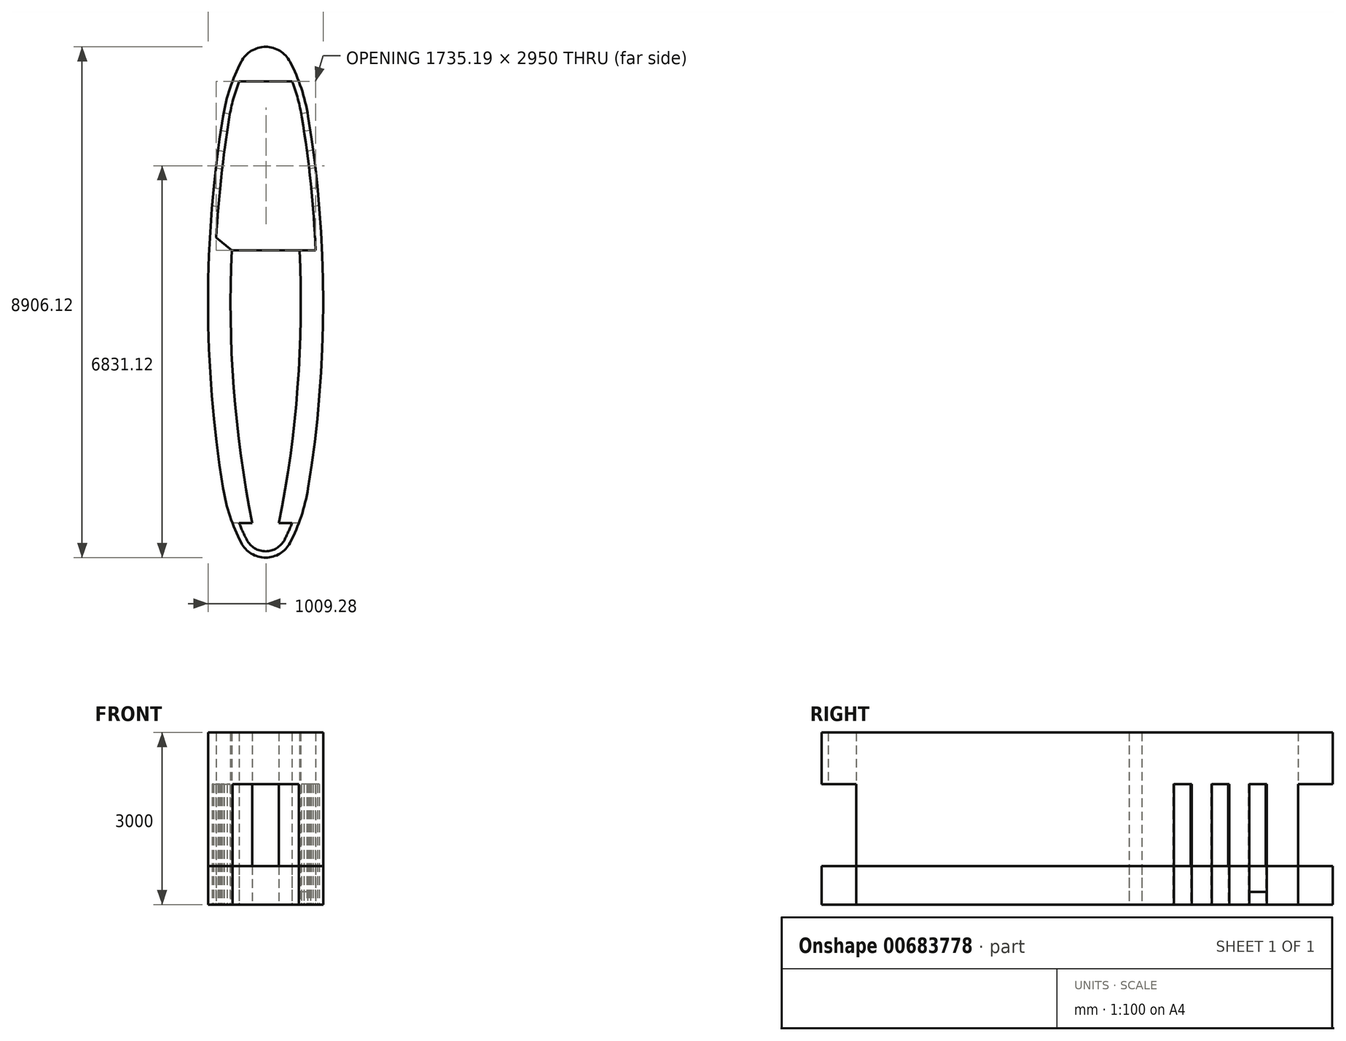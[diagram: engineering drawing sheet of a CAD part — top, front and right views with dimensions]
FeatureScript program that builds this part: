
annotation { "Feature Type Name" : "Feature", "Feature Type Description" : "" }
export const myFeature = defineFeature(function(context is Context, id is Id, definition is map)
    precondition{}
    {
        {
            var Q0;
            Q0=qCreatedBy(makeId("Top.planeOp"),FACE);
            var sketch = newSketch(context, id + "F0", { "sketchPlane" : qUnion([Q0])});
            skLineSegment(sketch, "E0", {"start": v(0, 4453.06) * mm, "end": v(0, -4453.06) * mm, "construction": true});
            skArc(sketch, "E1", {"start": v(426.3, 4193.68) * mm, "mid": v(249.5, 4383.12) * mm, "end": v(0, 4453.06) * mm});
            skArc(sketch, "E2", {"start": v(426.3, 4193.68) * mm, "mid": v(620.98, 3731.45) * mm, "end": v(740.57, 3244.35) * mm});
            skArc(sketch, "E3", {"start": v(740.57, 3244.35) * mm, "mid": v(937.75, 1627.5) * mm, "end": v(1003.62, 0) * mm});
            skArc(sketch, "E4.0", {"start": v(328.6, 4143.13) * mm, "mid": v(192.32, 4289.15) * mm, "end": v(0, 4343.06) * mm});
            skArc(sketch, "E4.1", {"start": v(328.6, 4143.13) * mm, "mid": v(516.55, 3696.88) * mm, "end": v(632, 3226.63) * mm});
            skArc(sketch, "E4.2", {"start": v(632, 3226.63) * mm, "mid": v(786.52, 2068.53) * mm, "end": v(873.24, 903.4) * mm});
            skLineSegment(sketch, "E5", {"start": v(1003.62, 0) * mm, "end": v(-1003.62, 0) * mm, "construction": true});
            skArc(sketch, "E6.MirrorCS", {"start": v(-740.57, 3244.35) * mm, "mid": v(-937.75, 1627.5) * mm, "end": v(-1003.62, 0) * mm});
            skArc(sketch, "E7.MirrorCS", {"start": v(-328.6, 4143.13) * mm, "mid": v(-516.55, 3696.88) * mm, "end": v(-632, 3226.63) * mm});
            skArc(sketch, "E8.MirrorCS", {"start": v(-426.3, 4193.68) * mm, "mid": v(-620.98, 3731.45) * mm, "end": v(-740.57, 3244.35) * mm});
            skArc(sketch, "E9.MirrorCS", {"start": v(-328.6, 4143.13) * mm, "mid": v(-192.32, 4289.15) * mm, "end": v(0, 4343.06) * mm});
            skArc(sketch, "E10.MirrorCS", {"start": v(-426.3, 4193.68) * mm, "mid": v(-249.5, 4383.12) * mm, "end": v(0, 4453.06) * mm});
            skLineSegment(sketch, "E11.MirrorCS", {"start": v(-1003.62, 0) * mm, "end": v(1003.62, 0) * mm, "construction": true});
            skArc(sketch, "E12.MirrorCS", {"start": v(-632, 3226.63) * mm, "mid": v(-786.53, 2068.37) * mm, "end": v(-873.25, 903.06) * mm});
            skArc(sketch, "E13.MirrorCS", {"start": v(632, -3226.63) * mm, "mid": v(828.11, -1618.61) * mm, "end": v(893.62, 0) * mm});
            skArc(sketch, "E14.MirrorCS", {"start": v(740.57, -3244.35) * mm, "mid": v(937.75, -1627.5) * mm, "end": v(1003.62, 0) * mm});
            skArc(sketch, "E15.MirrorCS", {"start": v(-632, -3226.63) * mm, "mid": v(-828.11, -1618.61) * mm, "end": v(-893.62, 0) * mm});
            skArc(sketch, "E16.MirrorCS", {"start": v(-740.57, -3244.35) * mm, "mid": v(-937.75, -1627.5) * mm, "end": v(-1003.62, 0) * mm});
            skArc(sketch, "E17.MirrorCS", {"start": v(328.6, -4143.13) * mm, "mid": v(516.55, -3696.88) * mm, "end": v(632, -3226.63) * mm});
            skArc(sketch, "E18.MirrorCS", {"start": v(426.3, -4193.68) * mm, "mid": v(620.98, -3731.45) * mm, "end": v(740.57, -3244.35) * mm});
            skArc(sketch, "E19.MirrorCS", {"start": v(-426.3, -4193.68) * mm, "mid": v(-620.98, -3731.45) * mm, "end": v(-740.57, -3244.35) * mm});
            skArc(sketch, "E20.MirrorCS", {"start": v(-328.6, -4143.13) * mm, "mid": v(-516.55, -3696.88) * mm, "end": v(-632, -3226.63) * mm});
            skArc(sketch, "E21.MirrorCS", {"start": v(-426.3, -4193.68) * mm, "mid": v(-249.5, -4383.12) * mm, "end": v(0, -4453.06) * mm});
            skArc(sketch, "E22.MirrorCS", {"start": v(-328.6, -4143.13) * mm, "mid": v(-192.32, -4289.15) * mm, "end": v(0, -4343.06) * mm});
            skArc(sketch, "E23.MirrorCS", {"start": v(328.6, -4143.13) * mm, "mid": v(192.32, -4289.15) * mm, "end": v(0, -4343.06) * mm});
            skArc(sketch, "E24.MirrorCS", {"start": v(426.3, -4193.68) * mm, "mid": v(249.5, -4383.12) * mm, "end": v(0, -4453.06) * mm});
            skLineSegment(sketch, "E25", {"start": v(577.97, 3853.06) * mm, "end": v(-577.97, 3853.06) * mm});
            skLineSegment(sketch, "E26", {"start": v(730.42, 3303.06) * mm, "end": v(621.9, 3285) * mm});
            skLineSegment(sketch, "E27", {"start": v(779.38, 2996.95) * mm, "end": v(670.86, 2978.88) * mm});
            skLineSegment(sketch, "E28", {"start": v(828.45, 2650.4) * mm, "end": v(719.89, 2632.34) * mm});
            skLineSegment(sketch, "E29", {"start": v(866.88, 2342.8) * mm, "end": v(758.25, 2324.72) * mm});
            skLineSegment(sketch, "E30", {"start": v(904.58, 1994.84) * mm, "end": v(795.83, 1976.74) * mm});
            skLineSegment(sketch, "E31", {"start": v(932.91, 1686.13) * mm, "end": v(824.04, 1668.03) * mm});
            skLineSegment(sketch, "E32.MirrorCS", {"start": v(-932.91, 1686.13) * mm, "end": v(-824.04, 1668.03) * mm});
            skLineSegment(sketch, "E33.MirrorCS", {"start": v(-904.58, 1994.84) * mm, "end": v(-795.83, 1976.74) * mm});
            skLineSegment(sketch, "E34.MirrorCS", {"start": v(-866.88, 2342.8) * mm, "end": v(-758.25, 2324.72) * mm});
            skLineSegment(sketch, "E35.MirrorCS", {"start": v(-828.45, 2650.4) * mm, "end": v(-719.89, 2632.34) * mm});
            skLineSegment(sketch, "E36.MirrorCS", {"start": v(-730.42, 3303.06) * mm, "end": v(-621.9, 3285) * mm});
            skLineSegment(sketch, "E37.MirrorCS", {"start": v(-779.38, 2996.95) * mm, "end": v(-670.86, 2978.88) * mm});
            skLineSegment(sketch, "E38", {"start": v(-873.25, 903.06) * mm, "end": v(-873.25, 903.06) * mm});
            skArc(sketch, "E39", {"start": v(873.24, 903.4) * mm, "mid": v(888.52, 451.81) * mm, "end": v(893.62, 0) * mm});
            skLineSegment(sketch, "E40", {"start": v(-873.25, 903.06) * mm, "end": v(873.25, 903.06) * mm});
            skArc(sketch, "E41", {"start": v(-873.25, 903.06) * mm, "mid": v(-888.53, 451.65) * mm, "end": v(-893.62, 0) * mm});
            skArc(sketch, "E42.0", {"start": v(-591.96, 903.06) * mm, "mid": v(-607.46, 451.65) * mm, "end": v(-612.62, 0) * mm});
            skArc(sketch, "E43.0", {"start": v(591.96, 903.06) * mm, "mid": v(607.46, 451.65) * mm, "end": v(612.62, 0) * mm});
            skArc(sketch, "E44.0", {"start": v(233.08, -3853.06) * mm, "mid": v(517.5, -1935.85) * mm, "end": v(612.62, 0) * mm});
            skArc(sketch, "E45.0", {"start": v(-233.08, -3853.06) * mm, "mid": v(-517.5, -1935.85) * mm, "end": v(-612.62, 0) * mm});
            skLineSegment(sketch, "E46", {"start": v(591.96, 903.06) * mm, "end": v(967.05, 1213.06) * mm});
            skLineSegment(sketch, "E47.MirrorCS", {"start": v(-591.96, 903.06) * mm, "end": v(-967.05, 1213.06) * mm});
            skLineSegment(sketch, "E48.MirrorCS", {"start": v(577.97, -3853.06) * mm, "end": v(-577.97, -3853.06) * mm});
            skSolve(sketch);
        }
        {
            var Q0;
            {var subQ20=sQuery(id+"F0.wireOp",EDGE,"E4.1");var subQ21=makeQuery(id+"F0.imprint","INTERSECT",VERTEX,{"derivedFrom":[subQ20,sQuery(id+"F0.wireOp",EDGE,"E26")]});Q0=makeQuery(id+"F0.imprint","IMPRINT",FACE,{"disambiguationData":[TD([[makeQuery(id+"F0.imprint","IMPRINT",EDGE,{"disambiguationData":[TD([[subQ21,1.0]])],"derivedFrom":subQ20}),-1.0]])]});}
            extrude(context, id + "F1", {"entities" : qUnion([Q0]), "depth" : 220 * mm, "offsetDistance" : 25 * mm});
        }
        {
            var Q0;
            {var subQ0=sQuery(id+"F0.wireOp",EDGE,"E30");Q0=makeQuery(id+"F0.imprint","IMPRINT",FACE,{"disambiguationData":[TD([[makeQuery(id+"F0.imprint","IMPRINT",EDGE,{"derivedFrom":subQ0}),1.0]])]});}
            var Q1;
            {var subQ0=sQuery(id+"F0.wireOp",EDGE,"E28");Q1=makeQuery(id+"F0.imprint","IMPRINT",FACE,{"disambiguationData":[TD([[makeQuery(id+"F0.imprint","IMPRINT",EDGE,{"derivedFrom":subQ0}),1.0]])]});}
            var Q2;
            {var subQ0=sQuery(id+"F0.wireOp",EDGE,"E29");Q2=makeQuery(id+"F0.imprint","IMPRINT",FACE,{"disambiguationData":[TD([[makeQuery(id+"F0.imprint","IMPRINT",EDGE,{"derivedFrom":subQ0}),1.0]])]});}
            var Q3;
            {var subQ0=sQuery(id+"F0.wireOp",EDGE,"E31");Q3=makeQuery(id+"F0.imprint","IMPRINT",FACE,{"disambiguationData":[TD([[makeQuery(id+"F0.imprint","IMPRINT",EDGE,{"derivedFrom":subQ0}),1.0]])]});}
            var Q4;
            {var subQ0=sQuery(id+"F0.wireOp",EDGE,"E13.MirrorCS");Q4=makeQuery(id+"F0.imprint","IMPRINT",FACE,{"disambiguationData":[TD([[makeQuery(id+"F0.imprint","IMPRINT",EDGE,{"derivedFrom":subQ0}),-1.0]])]});}
            var Q5;
            {var subQ0=sQuery(id+"F0.wireOp",EDGE,"E39");var subQ1=sQuery(id+"F0.wireOp",EDGE,"E4.2");var subQ2=makeQuery(id+"F0.imprint","INTERSECT",VERTEX,{"derivedFrom":[subQ1,subQ0]});Q5=makeQuery(id+"F0.imprint","IMPRINT",FACE,{"disambiguationData":[TD([[makeQuery(id+"F0.imprint","IMPRINT",EDGE,{"disambiguationData":[TD([[subQ2,1.0]])],"derivedFrom":subQ1}),-1.0]])]});}
            var Q6;
            {var subQ1=sQuery(id+"F0.wireOp",EDGE,"E13.MirrorCS");Q6=makeQuery(id+"F0.imprint","IMPRINT",FACE,{"disambiguationData":[TD([[makeQuery(id+"F0.imprint","IMPRINT",EDGE,{"derivedFrom":subQ1}),1.0]])]});}
            var Q7;
            {var subQ1=sQuery(id+"F0.wireOp",EDGE,"E42.0");Q7=makeQuery(id+"F0.imprint","IMPRINT",FACE,{"disambiguationData":[TD([[makeQuery(id+"F0.imprint","IMPRINT",EDGE,{"derivedFrom":subQ1}),1.0]])]});}
            var Q8;
            {var subQ4=sQuery(id+"F0.wireOp",EDGE,"E15.MirrorCS");Q8=makeQuery(id+"F0.imprint","IMPRINT",FACE,{"disambiguationData":[TD([[makeQuery(id+"F0.imprint","IMPRINT",EDGE,{"derivedFrom":subQ4}),-1.0]])]});}
            var Q9;
            {var subQ1=sQuery(id+"F0.wireOp",EDGE,"E12.MirrorCS");var subQ3=sQuery(id+"F0.wireOp",EDGE,"E47.MirrorCS");var subQ4=makeQuery(id+"F0.imprint","INTERSECT",VERTEX,{"derivedFrom":[subQ1,subQ3]});Q9=makeQuery(id+"F0.imprint","IMPRINT",FACE,{"disambiguationData":[TD([[makeQuery(id+"F0.imprint","IMPRINT",EDGE,{"disambiguationData":[TD([[subQ4,-1.0]])],"derivedFrom":subQ1}),1.0]])]});}
            var Q10;
            {var subQ2=sQuery(id+"F0.wireOp",EDGE,"E15.MirrorCS");Q10=makeQuery(id+"F0.imprint","IMPRINT",FACE,{"disambiguationData":[TD([[makeQuery(id+"F0.imprint","IMPRINT",EDGE,{"derivedFrom":subQ2}),1.0]])]});}
            var Q11;
            {var subQ0=sQuery(id+"F0.wireOp",EDGE,"E22.MirrorCS");Q11=makeQuery(id+"F0.imprint","IMPRINT",FACE,{"disambiguationData":[TD([[makeQuery(id+"F0.imprint","IMPRINT",EDGE,{"derivedFrom":subQ0}),1.0]])]});}
            var Q12;
            {var subQ4=sQuery(id+"F0.wireOp",EDGE,"E21.MirrorCS");Q12=makeQuery(id+"F0.imprint","IMPRINT",FACE,{"disambiguationData":[TD([[makeQuery(id+"F0.imprint","IMPRINT",EDGE,{"derivedFrom":subQ4}),1.0]])]});}
            var Q13;
            {var subQ5=sQuery(id+"F0.wireOp",EDGE,"E4.0");Q13=makeQuery(id+"F0.imprint","IMPRINT",FACE,{"disambiguationData":[TD([[makeQuery(id+"F0.imprint","IMPRINT",EDGE,{"derivedFrom":subQ5}),1.0]])]});}
            var Q14;
            {var subQ5=sQuery(id+"F0.wireOp",EDGE,"E1");Q14=makeQuery(id+"F0.imprint","IMPRINT",FACE,{"disambiguationData":[TD([[makeQuery(id+"F0.imprint","IMPRINT",EDGE,{"derivedFrom":subQ5}),1.0]])]});}
            var Q15;
            {var subQ3=sQuery(id+"F0.wireOp",EDGE,"E26");Q15=makeQuery(id+"F0.imprint","IMPRINT",FACE,{"disambiguationData":[TD([[makeQuery(id+"F0.imprint","IMPRINT",EDGE,{"derivedFrom":subQ3}),-1.0]])]});}
            var Q16;
            {var subQ7=sQuery(id+"F0.wireOp",EDGE,"E26");Q16=makeQuery(id+"F0.imprint","IMPRINT",FACE,{"disambiguationData":[TD([[makeQuery(id+"F0.imprint","IMPRINT",EDGE,{"derivedFrom":subQ7}),1.0]])]});}
            var Q17;
            {var subQ0=sQuery(id+"F0.wireOp",EDGE,"E27");Q17=makeQuery(id+"F0.imprint","IMPRINT",FACE,{"disambiguationData":[TD([[makeQuery(id+"F0.imprint","IMPRINT",EDGE,{"derivedFrom":subQ0}),1.0]])]});}
            var Q18;
            {var subQ0=sQuery(id+"F0.wireOp",EDGE,"E36.MirrorCS");Q18=makeQuery(id+"F0.imprint","IMPRINT",FACE,{"disambiguationData":[TD([[makeQuery(id+"F0.imprint","IMPRINT",EDGE,{"derivedFrom":subQ0}),1.0]])]});}
            var Q19;
            {var subQ3=sQuery(id+"F0.wireOp",EDGE,"E36.MirrorCS");Q19=makeQuery(id+"F0.imprint","IMPRINT",FACE,{"disambiguationData":[TD([[makeQuery(id+"F0.imprint","IMPRINT",EDGE,{"derivedFrom":subQ3}),-1.0]])]});}
            var Q20;
            {var subQ0=sQuery(id+"F0.wireOp",EDGE,"E35.MirrorCS");Q20=makeQuery(id+"F0.imprint","IMPRINT",FACE,{"disambiguationData":[TD([[makeQuery(id+"F0.imprint","IMPRINT",EDGE,{"derivedFrom":subQ0}),1.0]])]});}
            var Q21;
            {var subQ0=sQuery(id+"F0.wireOp",EDGE,"E34.MirrorCS");Q21=makeQuery(id+"F0.imprint","IMPRINT",FACE,{"disambiguationData":[TD([[makeQuery(id+"F0.imprint","IMPRINT",EDGE,{"derivedFrom":subQ0}),1.0]])]});}
            var Q22;
            {var subQ0=sQuery(id+"F0.wireOp",EDGE,"E33.MirrorCS");Q22=makeQuery(id+"F0.imprint","IMPRINT",FACE,{"disambiguationData":[TD([[makeQuery(id+"F0.imprint","IMPRINT",EDGE,{"derivedFrom":subQ0}),1.0]])]});}
            var Q23;
            {var subQ0=sQuery(id+"F0.wireOp",EDGE,"E32.MirrorCS");Q23=makeQuery(id+"F0.imprint","IMPRINT",FACE,{"disambiguationData":[TD([[makeQuery(id+"F0.imprint","IMPRINT",EDGE,{"derivedFrom":subQ0}),1.0]])]});}
            var Q24;
            {var subQ0=sQuery(id+"F0.wireOp",EDGE,"E32.MirrorCS");Q24=makeQuery(id+"F0.imprint","IMPRINT",FACE,{"disambiguationData":[TD([[makeQuery(id+"F0.imprint","IMPRINT",EDGE,{"derivedFrom":subQ0}),-1.0]])]});}
            extrude(context, id + "F2", {"entities" : qUnion([Q0, Q1, Q2, Q3, Q4, Q5, Q6, Q7, Q8, Q9, Q10, Q11, Q12, Q13, Q14, Q15, Q16, Q17, Q18, Q19, Q20, Q21, Q22, Q23, Q24]), "depth" : 670 * mm, "offsetDistance" : 25 * mm});
        }
        {
            var Q0;
            {var subQ0=sQuery(id+"F0.wireOp",EDGE,"E31");Q0=makeQuery(id+"F0.imprint","IMPRINT",FACE,{"disambiguationData":[TD([[makeQuery(id+"F0.imprint","IMPRINT",EDGE,{"derivedFrom":subQ0}),1.0]])]});}
            var Q1;
            {var subQ0=sQuery(id+"F0.wireOp",EDGE,"E13.MirrorCS");Q1=makeQuery(id+"F0.imprint","IMPRINT",FACE,{"disambiguationData":[TD([[makeQuery(id+"F0.imprint","IMPRINT",EDGE,{"derivedFrom":subQ0}),-1.0]])]});}
            var Q2;
            {var subQ0=sQuery(id+"F0.wireOp",EDGE,"E39");var subQ1=sQuery(id+"F0.wireOp",EDGE,"E4.2");var subQ2=makeQuery(id+"F0.imprint","INTERSECT",VERTEX,{"derivedFrom":[subQ1,subQ0]});Q2=makeQuery(id+"F0.imprint","IMPRINT",FACE,{"disambiguationData":[TD([[makeQuery(id+"F0.imprint","IMPRINT",EDGE,{"disambiguationData":[TD([[subQ2,1.0]])],"derivedFrom":subQ1}),-1.0]])]});}
            var Q3;
            {var subQ1=sQuery(id+"F0.wireOp",EDGE,"E13.MirrorCS");Q3=makeQuery(id+"F0.imprint","IMPRINT",FACE,{"disambiguationData":[TD([[makeQuery(id+"F0.imprint","IMPRINT",EDGE,{"derivedFrom":subQ1}),1.0]])]});}
            var Q4;
            {var subQ4=sQuery(id+"F0.wireOp",EDGE,"E15.MirrorCS");Q4=makeQuery(id+"F0.imprint","IMPRINT",FACE,{"disambiguationData":[TD([[makeQuery(id+"F0.imprint","IMPRINT",EDGE,{"derivedFrom":subQ4}),-1.0]])]});}
            var Q5;
            {var subQ2=sQuery(id+"F0.wireOp",EDGE,"E15.MirrorCS");Q5=makeQuery(id+"F0.imprint","IMPRINT",FACE,{"disambiguationData":[TD([[makeQuery(id+"F0.imprint","IMPRINT",EDGE,{"derivedFrom":subQ2}),1.0]])]});}
            var Q6;
            {var subQ1=sQuery(id+"F0.wireOp",EDGE,"E12.MirrorCS");var subQ3=sQuery(id+"F0.wireOp",EDGE,"E47.MirrorCS");var subQ4=makeQuery(id+"F0.imprint","INTERSECT",VERTEX,{"derivedFrom":[subQ1,subQ3]});Q6=makeQuery(id+"F0.imprint","IMPRINT",FACE,{"disambiguationData":[TD([[makeQuery(id+"F0.imprint","IMPRINT",EDGE,{"disambiguationData":[TD([[subQ4,-1.0]])],"derivedFrom":subQ1}),1.0]])]});}
            var Q7;
            {var subQ0=sQuery(id+"F0.wireOp",EDGE,"E29");Q7=makeQuery(id+"F0.imprint","IMPRINT",FACE,{"disambiguationData":[TD([[makeQuery(id+"F0.imprint","IMPRINT",EDGE,{"derivedFrom":subQ0}),1.0]])]});}
            var Q8;
            {var subQ0=sQuery(id+"F0.wireOp",EDGE,"E27");Q8=makeQuery(id+"F0.imprint","IMPRINT",FACE,{"disambiguationData":[TD([[makeQuery(id+"F0.imprint","IMPRINT",EDGE,{"derivedFrom":subQ0}),1.0]])]});}
            var Q9;
            {var subQ3=sQuery(id+"F0.wireOp",EDGE,"E26");Q9=makeQuery(id+"F0.imprint","IMPRINT",FACE,{"disambiguationData":[TD([[makeQuery(id+"F0.imprint","IMPRINT",EDGE,{"derivedFrom":subQ3}),-1.0]])]});}
            var Q10;
            {var subQ0=sQuery(id+"F0.wireOp",EDGE,"E32.MirrorCS");Q10=makeQuery(id+"F0.imprint","IMPRINT",FACE,{"disambiguationData":[TD([[makeQuery(id+"F0.imprint","IMPRINT",EDGE,{"derivedFrom":subQ0}),-1.0]])]});}
            var Q11;
            {var subQ0=sQuery(id+"F0.wireOp",EDGE,"E33.MirrorCS");Q11=makeQuery(id+"F0.imprint","IMPRINT",FACE,{"disambiguationData":[TD([[makeQuery(id+"F0.imprint","IMPRINT",EDGE,{"derivedFrom":subQ0}),1.0]])]});}
            var Q12;
            {var subQ0=sQuery(id+"F0.wireOp",EDGE,"E35.MirrorCS");Q12=makeQuery(id+"F0.imprint","IMPRINT",FACE,{"disambiguationData":[TD([[makeQuery(id+"F0.imprint","IMPRINT",EDGE,{"derivedFrom":subQ0}),1.0]])]});}
            var Q13;
            {var subQ0=sQuery(id+"F0.wireOp",EDGE,"E36.MirrorCS");Q13=makeQuery(id+"F0.imprint","IMPRINT",FACE,{"disambiguationData":[TD([[makeQuery(id+"F0.imprint","IMPRINT",EDGE,{"derivedFrom":subQ0}),1.0]])]});}
            extrude(context, id + "F3", {"entities" : qUnion([Q0, Q1, Q2, Q3, Q4, Q5, Q6, Q7, Q8, Q9, Q10, Q11, Q12, Q13]), "depth" : 2100 * mm, "offsetDistance" : 25 * mm});
        }
        {
            var Q0;
            Q0=makeQuery(id+"F3.opExtrude","CAP_FACE",FACE,{"disambiguationData":[OSD([sQuery(id+"F0.wireOp",EDGE,"E3"),sQuery(id+"F0.wireOp",EDGE,"E4.2"),sQuery(id+"F0.wireOp",EDGE,"E14.MirrorCS"),sQuery(id+"F0.wireOp",EDGE,"E18.MirrorCS"),sQuery(id+"F0.wireOp",EDGE,"E31"),sQuery(id+"F0.wireOp",EDGE,"E43.0"),sQuery(id+"F0.wireOp",EDGE,"E44.0"),sQuery(id+"F0.wireOp",EDGE,"E46"),sQuery(id+"F0.wireOp",EDGE,"E48.MirrorCS")])],"isStart":false});
            var sketch = newSketch(context, id + "F4", { "sketchPlane" : qUnion([Q0])});
            skLineSegment(sketch, "E49", {"start": v(0, 4453.06) * mm, "end": v(0, -4453.06) * mm, "construction": true});
            skArc(sketch, "E50", {"start": v(426.3, 4193.68) * mm, "mid": v(249.5, 4383.12) * mm, "end": v(0, 4453.06) * mm});
            skArc(sketch, "E51", {"start": v(426.3, 4193.68) * mm, "mid": v(620.98, 3731.45) * mm, "end": v(740.57, 3244.35) * mm});
            skArc(sketch, "E52", {"start": v(740.57, 3244.35) * mm, "mid": v(937.75, 1627.5) * mm, "end": v(1003.62, 0) * mm});
            skArc(sketch, "E53.0", {"start": v(328.6, 4143.13) * mm, "mid": v(192.32, 4289.15) * mm, "end": v(0, 4343.06) * mm});
            skArc(sketch, "E53.1", {"start": v(328.6, 4143.13) * mm, "mid": v(516.55, 3696.88) * mm, "end": v(632, 3226.63) * mm});
            skArc(sketch, "E53.2", {"start": v(632, 3226.63) * mm, "mid": v(786.52, 2068.53) * mm, "end": v(873.24, 903.4) * mm});
            skLineSegment(sketch, "E54", {"start": v(1003.62, 0) * mm, "end": v(-1788.8, 0) * mm, "construction": true});
            skArc(sketch, "E55.MirrorCS", {"start": v(-740.57, 3244.35) * mm, "mid": v(-937.75, 1627.5) * mm, "end": v(-1003.62, 0) * mm});
            skArc(sketch, "E56.MirrorCS", {"start": v(-328.6, 4143.13) * mm, "mid": v(-516.55, 3696.88) * mm, "end": v(-632, 3226.63) * mm});
            skArc(sketch, "E57.MirrorCS", {"start": v(-426.3, 4193.68) * mm, "mid": v(-620.98, 3731.45) * mm, "end": v(-740.57, 3244.35) * mm});
            skArc(sketch, "E58.MirrorCS", {"start": v(-328.6, 4143.13) * mm, "mid": v(-192.32, 4289.15) * mm, "end": v(0, 4343.06) * mm});
            skArc(sketch, "E59.MirrorCS", {"start": v(-426.3, 4193.68) * mm, "mid": v(-249.5, 4383.12) * mm, "end": v(0, 4453.06) * mm});
            skLineSegment(sketch, "E60.MirrorCS", {"start": v(-1003.62, 0) * mm, "end": v(1788.8, 0) * mm, "construction": true});
            skArc(sketch, "E61.MirrorCS", {"start": v(-632, 3226.63) * mm, "mid": v(-786.53, 2068.37) * mm, "end": v(-873.25, 903.06) * mm});
            skArc(sketch, "E62.MirrorCS", {"start": v(632, -3226.63) * mm, "mid": v(828.11, -1618.61) * mm, "end": v(893.62, 0) * mm});
            skArc(sketch, "E63.MirrorCS", {"start": v(740.57, -3244.35) * mm, "mid": v(937.75, -1627.5) * mm, "end": v(1003.62, 0) * mm});
            skArc(sketch, "E64.MirrorCS", {"start": v(-632, -3226.63) * mm, "mid": v(-828.11, -1618.61) * mm, "end": v(-893.62, 0) * mm});
            skArc(sketch, "E65.MirrorCS", {"start": v(-740.57, -3244.35) * mm, "mid": v(-937.75, -1627.5) * mm, "end": v(-1003.62, 0) * mm});
            skArc(sketch, "E66.MirrorCS", {"start": v(328.6, -4143.13) * mm, "mid": v(516.55, -3696.88) * mm, "end": v(632, -3226.63) * mm});
            skArc(sketch, "E67.MirrorCS", {"start": v(426.3, -4193.68) * mm, "mid": v(620.98, -3731.45) * mm, "end": v(740.57, -3244.35) * mm});
            skArc(sketch, "E68.MirrorCS", {"start": v(-426.3, -4193.68) * mm, "mid": v(-620.98, -3731.45) * mm, "end": v(-740.57, -3244.35) * mm});
            skArc(sketch, "E69.MirrorCS", {"start": v(-328.6, -4143.13) * mm, "mid": v(-516.55, -3696.88) * mm, "end": v(-632, -3226.63) * mm});
            skArc(sketch, "E70.MirrorCS", {"start": v(-426.3, -4193.68) * mm, "mid": v(-249.5, -4383.12) * mm, "end": v(0, -4453.06) * mm});
            skArc(sketch, "E71.MirrorCS", {"start": v(-328.6, -4143.13) * mm, "mid": v(-192.32, -4289.15) * mm, "end": v(0, -4343.06) * mm});
            skArc(sketch, "E72.MirrorCS", {"start": v(328.6, -4143.13) * mm, "mid": v(192.32, -4289.15) * mm, "end": v(0, -4343.06) * mm});
            skArc(sketch, "E73.MirrorCS", {"start": v(426.3, -4193.68) * mm, "mid": v(249.5, -4383.12) * mm, "end": v(0, -4453.06) * mm});
            skLineSegment(sketch, "E74", {"start": v(577.97, 3853.06) * mm, "end": v(-577.97, 3853.06) * mm});
            skLineSegment(sketch, "E75", {"start": v(730.42, 3303.06) * mm, "end": v(621.9, 3285) * mm});
            skLineSegment(sketch, "E76", {"start": v(779.38, 2996.95) * mm, "end": v(670.86, 2978.88) * mm});
            skLineSegment(sketch, "E77", {"start": v(828.45, 2650.4) * mm, "end": v(719.89, 2632.34) * mm});
            skLineSegment(sketch, "E78", {"start": v(866.88, 2342.8) * mm, "end": v(758.25, 2324.72) * mm});
            skLineSegment(sketch, "E79", {"start": v(904.58, 1994.84) * mm, "end": v(795.83, 1976.74) * mm});
            skLineSegment(sketch, "E80", {"start": v(932.91, 1686.13) * mm, "end": v(824.04, 1668.03) * mm});
            skLineSegment(sketch, "E81.MirrorCS", {"start": v(-932.91, 1686.13) * mm, "end": v(-824.04, 1668.03) * mm});
            skLineSegment(sketch, "E82.MirrorCS", {"start": v(-904.58, 1994.84) * mm, "end": v(-795.83, 1976.74) * mm});
            skLineSegment(sketch, "E83.MirrorCS", {"start": v(-866.88, 2342.8) * mm, "end": v(-758.25, 2324.72) * mm});
            skLineSegment(sketch, "E84.MirrorCS", {"start": v(-828.45, 2650.4) * mm, "end": v(-719.89, 2632.34) * mm});
            skLineSegment(sketch, "E85.MirrorCS", {"start": v(-730.42, 3303.06) * mm, "end": v(-621.9, 3285) * mm});
            skLineSegment(sketch, "E86.MirrorCS", {"start": v(-779.38, 2996.95) * mm, "end": v(-670.86, 2978.88) * mm});
            skLineSegment(sketch, "E87", {"start": v(-873.25, 903.06) * mm, "end": v(-873.25, 903.06) * mm});
            skArc(sketch, "E88", {"start": v(873.24, 903.4) * mm, "mid": v(888.52, 451.81) * mm, "end": v(893.62, 0) * mm});
            skLineSegment(sketch, "E89", {"start": v(-873.25, 903.06) * mm, "end": v(873.25, 903.06) * mm});
            skArc(sketch, "E90", {"start": v(-873.25, 903.06) * mm, "mid": v(-888.53, 451.65) * mm, "end": v(-893.62, 0) * mm});
            skArc(sketch, "E91.0", {"start": v(-591.96, 903.06) * mm, "mid": v(-607.46, 451.65) * mm, "end": v(-612.62, 0) * mm});
            skArc(sketch, "E92.0", {"start": v(591.96, 903.06) * mm, "mid": v(607.46, 451.65) * mm, "end": v(612.62, 0) * mm});
            skArc(sketch, "E93.0", {"start": v(233.08, -3853.06) * mm, "mid": v(517.5, -1935.85) * mm, "end": v(612.62, 0) * mm});
            skArc(sketch, "E94.0", {"start": v(-233.08, -3853.06) * mm, "mid": v(-517.5, -1935.85) * mm, "end": v(-612.62, 0) * mm});
            skLineSegment(sketch, "E95", {"start": v(591.96, 903.06) * mm, "end": v(967.05, 1213.06) * mm});
            skLineSegment(sketch, "E96.MirrorCS", {"start": v(-591.96, 903.06) * mm, "end": v(-967.05, 1213.06) * mm});
            skLineSegment(sketch, "E97.MirrorCS", {"start": v(577.97, -3853.06) * mm, "end": v(-577.97, -3853.06) * mm});
            skSolve(sketch);
        }
        {
            var Q0;
            {var subQ1=sQuery(id+"F4.wireOp",EDGE,"E62.MirrorCS");Q0=makeQuery(id+"F4.imprint","IMPRINT",FACE,{"disambiguationData":[TD([[makeQuery(id+"F4.imprint","IMPRINT",EDGE,{"derivedFrom":subQ1}),1.0]])]});}
            var Q1;
            {var subQ0=sQuery(id+"F4.wireOp",EDGE,"E62.MirrorCS");Q1=makeQuery(id+"F4.imprint","IMPRINT",FACE,{"disambiguationData":[TD([[makeQuery(id+"F4.imprint","IMPRINT",EDGE,{"derivedFrom":subQ0}),-1.0]])]});}
            var Q2;
            {var subQ0=sQuery(id+"F4.wireOp",EDGE,"E95");var subQ1=sQuery(id+"F4.wireOp",EDGE,"E53.2");var subQ2=makeQuery(id+"F4.imprint","INTERSECT",VERTEX,{"derivedFrom":[subQ1,subQ0]});Q2=makeQuery(id+"F4.imprint","IMPRINT",FACE,{"disambiguationData":[TD([[makeQuery(id+"F4.imprint","IMPRINT",EDGE,{"disambiguationData":[TD([[subQ2,-1.0]])],"derivedFrom":subQ1}),-1.0]])]});}
            var Q3;
            {var subQ4=sQuery(id+"F4.wireOp",EDGE,"E64.MirrorCS");Q3=makeQuery(id+"F4.imprint","IMPRINT",FACE,{"disambiguationData":[TD([[makeQuery(id+"F4.imprint","IMPRINT",EDGE,{"derivedFrom":subQ4}),-1.0]])]});}
            var Q4;
            {var subQ2=sQuery(id+"F4.wireOp",EDGE,"E64.MirrorCS");Q4=makeQuery(id+"F4.imprint","IMPRINT",FACE,{"disambiguationData":[TD([[makeQuery(id+"F4.imprint","IMPRINT",EDGE,{"derivedFrom":subQ2}),1.0]])]});}
            var Q5;
            {var subQ1=sQuery(id+"F4.wireOp",EDGE,"E61.MirrorCS");var subQ3=sQuery(id+"F4.wireOp",EDGE,"E96.MirrorCS");var subQ4=makeQuery(id+"F4.imprint","INTERSECT",VERTEX,{"derivedFrom":[subQ1,subQ3]});Q5=makeQuery(id+"F4.imprint","IMPRINT",FACE,{"disambiguationData":[TD([[makeQuery(id+"F4.imprint","IMPRINT",EDGE,{"disambiguationData":[TD([[subQ4,-1.0]])],"derivedFrom":subQ1}),1.0]])]});}
            var Q6;
            {var subQ4=sQuery(id+"F4.wireOp",EDGE,"E70.MirrorCS");Q6=makeQuery(id+"F4.imprint","IMPRINT",FACE,{"disambiguationData":[TD([[makeQuery(id+"F4.imprint","IMPRINT",EDGE,{"derivedFrom":subQ4}),1.0]])]});}
            var Q7;
            {var subQ0=sQuery(id+"F4.wireOp",EDGE,"E81.MirrorCS");Q7=makeQuery(id+"F4.imprint","IMPRINT",FACE,{"disambiguationData":[TD([[makeQuery(id+"F4.imprint","IMPRINT",EDGE,{"derivedFrom":subQ0}),-1.0]])]});}
            var Q8;
            {var subQ0=sQuery(id+"F4.wireOp",EDGE,"E81.MirrorCS");Q8=makeQuery(id+"F4.imprint","IMPRINT",FACE,{"disambiguationData":[TD([[makeQuery(id+"F4.imprint","IMPRINT",EDGE,{"derivedFrom":subQ0}),1.0]])]});}
            var Q9;
            {var subQ0=sQuery(id+"F4.wireOp",EDGE,"E82.MirrorCS");Q9=makeQuery(id+"F4.imprint","IMPRINT",FACE,{"disambiguationData":[TD([[makeQuery(id+"F4.imprint","IMPRINT",EDGE,{"derivedFrom":subQ0}),1.0]])]});}
            var Q10;
            {var subQ0=sQuery(id+"F4.wireOp",EDGE,"E83.MirrorCS");Q10=makeQuery(id+"F4.imprint","IMPRINT",FACE,{"disambiguationData":[TD([[makeQuery(id+"F4.imprint","IMPRINT",EDGE,{"derivedFrom":subQ0}),1.0]])]});}
            var Q11;
            {var subQ0=sQuery(id+"F4.wireOp",EDGE,"E84.MirrorCS");Q11=makeQuery(id+"F4.imprint","IMPRINT",FACE,{"disambiguationData":[TD([[makeQuery(id+"F4.imprint","IMPRINT",EDGE,{"derivedFrom":subQ0}),1.0]])]});}
            var Q12;
            {var subQ0=sQuery(id+"F4.wireOp",EDGE,"E80");Q12=makeQuery(id+"F4.imprint","IMPRINT",FACE,{"disambiguationData":[TD([[makeQuery(id+"F4.imprint","IMPRINT",EDGE,{"derivedFrom":subQ0}),1.0]])]});}
            var Q13;
            {var subQ2=sQuery(id+"F4.wireOp",EDGE,"E79");Q13=makeQuery(id+"F4.imprint","IMPRINT",FACE,{"disambiguationData":[TD([[makeQuery(id+"F4.imprint","IMPRINT",EDGE,{"derivedFrom":subQ2}),1.0]])]});}
            var Q14;
            {var subQ0=sQuery(id+"F4.wireOp",EDGE,"E78");Q14=makeQuery(id+"F4.imprint","IMPRINT",FACE,{"disambiguationData":[TD([[makeQuery(id+"F4.imprint","IMPRINT",EDGE,{"derivedFrom":subQ0}),1.0]])]});}
            var Q15;
            {var subQ0=sQuery(id+"F4.wireOp",EDGE,"E77");Q15=makeQuery(id+"F4.imprint","IMPRINT",FACE,{"disambiguationData":[TD([[makeQuery(id+"F4.imprint","IMPRINT",EDGE,{"derivedFrom":subQ0}),1.0]])]});}
            var Q16;
            {var subQ0=sQuery(id+"F4.wireOp",EDGE,"E76");Q16=makeQuery(id+"F4.imprint","IMPRINT",FACE,{"disambiguationData":[TD([[makeQuery(id+"F4.imprint","IMPRINT",EDGE,{"derivedFrom":subQ0}),1.0]])]});}
            var Q17;
            {var subQ7=sQuery(id+"F4.wireOp",EDGE,"E75");Q17=makeQuery(id+"F4.imprint","IMPRINT",FACE,{"disambiguationData":[TD([[makeQuery(id+"F4.imprint","IMPRINT",EDGE,{"derivedFrom":subQ7}),1.0]])]});}
            var Q18;
            {var subQ3=sQuery(id+"F4.wireOp",EDGE,"E75");Q18=makeQuery(id+"F4.imprint","IMPRINT",FACE,{"disambiguationData":[TD([[makeQuery(id+"F4.imprint","IMPRINT",EDGE,{"derivedFrom":subQ3}),-1.0]])]});}
            var Q19;
            {var subQ3=sQuery(id+"F4.wireOp",EDGE,"E85.MirrorCS");Q19=makeQuery(id+"F4.imprint","IMPRINT",FACE,{"disambiguationData":[TD([[makeQuery(id+"F4.imprint","IMPRINT",EDGE,{"derivedFrom":subQ3}),-1.0]])]});}
            var Q20;
            {var subQ0=sQuery(id+"F4.wireOp",EDGE,"E85.MirrorCS");Q20=makeQuery(id+"F4.imprint","IMPRINT",FACE,{"disambiguationData":[TD([[makeQuery(id+"F4.imprint","IMPRINT",EDGE,{"derivedFrom":subQ0}),1.0]])]});}
            var Q21;
            {var subQ5=sQuery(id+"F4.wireOp",EDGE,"E53.0");Q21=makeQuery(id+"F4.imprint","IMPRINT",FACE,{"disambiguationData":[TD([[makeQuery(id+"F4.imprint","IMPRINT",EDGE,{"derivedFrom":subQ5}),1.0]])]});}
            var Q22;
            {var subQ5=sQuery(id+"F4.wireOp",EDGE,"E50");Q22=makeQuery(id+"F4.imprint","IMPRINT",FACE,{"disambiguationData":[TD([[makeQuery(id+"F4.imprint","IMPRINT",EDGE,{"derivedFrom":subQ5}),1.0]])]});}
            extrude(context, id + "F5", {"entities" : qUnion([Q0, Q1, Q2, Q3, Q4, Q5, Q6, Q7, Q8, Q9, Q10, Q11, Q12, Q13, Q14, Q15, Q16, Q17, Q18, Q19, Q20, Q21, Q22]), "operationType" : NewBodyOperationType.ADD, "depth" : 900 * mm, "offsetDistance" : 25 * mm});
        }
    });
